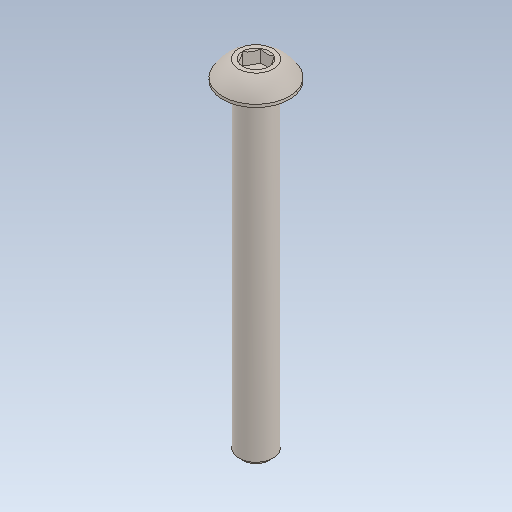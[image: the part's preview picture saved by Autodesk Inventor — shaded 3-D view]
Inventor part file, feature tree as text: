
AUTODESK INVENTOR PART (.ipt)
format: ipt  version: 2020 (Build 240168000, 168)  size: 112,128 bytes
history: native  units: in
note: dims shown in document units (in); Inventor stores cm internally (conversion verified against a paired STEP export)
features: fillet x1
ambient origin geometry x8: Origin, YZ Plane, XZ Plane, XY Plane, X Axis, Y Axis, Z Axis, Center Point
bodies: Solid1 (feature_tree)
feature tree (1):
  fillet  "Fillet1"  [1 undecoded]
note: 1 required parameter value undecoded (feature->parameter linkage not recoverable at this tier; creation-order binding heuristic only, values carry confidence <= 0.55)
